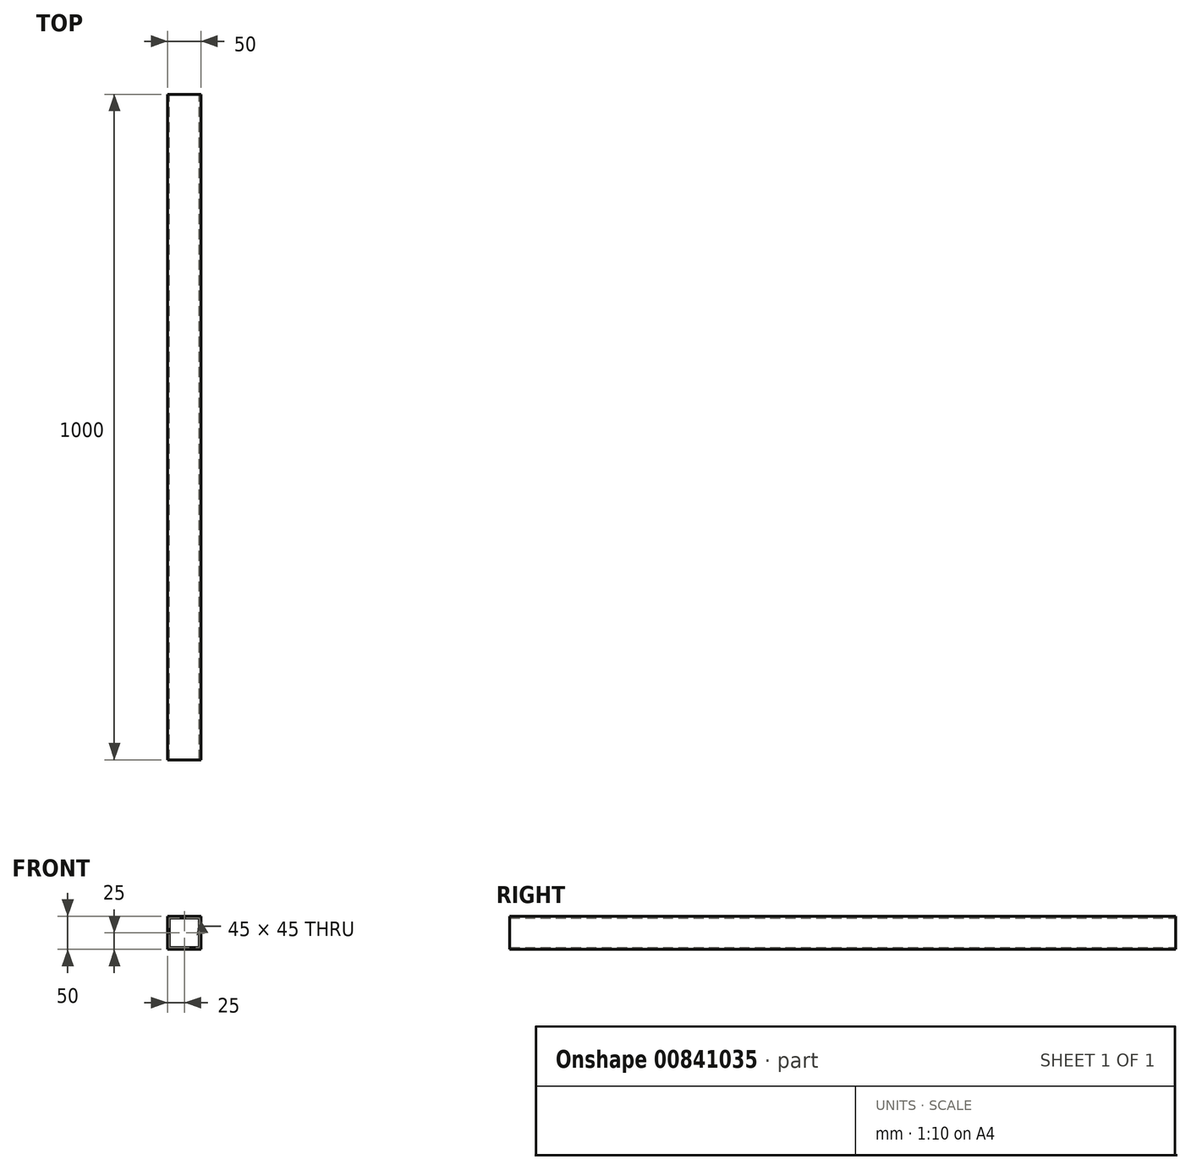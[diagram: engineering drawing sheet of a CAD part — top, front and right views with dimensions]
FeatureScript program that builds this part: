
annotation { "Feature Type Name" : "Feature", "Feature Type Description" : "" }
export const myFeature = defineFeature(function(context is Context, id is Id, definition is map)
    precondition{}
    {
        {
            var Q0;
            Q0=qCreatedBy(makeId("Front.planeOp"),FACE);
            var sketch = newSketch(context, id + "F0", { "sketchPlane" : qUnion([Q0])});
            skLineSegment(sketch, "E0.top", {"start": v(0, 25) * mm, "end": v(25, 25) * mm});
            skLineSegment(sketch, "E0.right", {"start": v(25, 0) * mm, "end": v(25, 25) * mm});
            skLineSegment(sketch, "E1.MirrorCS", {"start": v(0, 25) * mm, "end": v(-25, 25) * mm});
            skLineSegment(sketch, "E2.MirrorCS", {"start": v(-25, 0) * mm, "end": v(-25, 25) * mm});
            skLineSegment(sketch, "E3.MirrorCS", {"start": v(-25, 0) * mm, "end": v(-25, -25) * mm});
            skLineSegment(sketch, "E4.MirrorCS", {"start": v(0, -25) * mm, "end": v(-25, -25) * mm});
            skLineSegment(sketch, "E5.MirrorCS", {"start": v(0, -25) * mm, "end": v(25, -25) * mm});
            skLineSegment(sketch, "E6.MirrorCS", {"start": v(25, 0) * mm, "end": v(25, -25) * mm});
            skLineSegment(sketch, "E7", {"start": v(0, 0) * mm, "end": v(-75.09, 0) * mm});
            skSolve(sketch);
        }
        {
            var Q0;
            Q0 = qSketchRegion(id + "F0", true);
            extrude(context, id + "F1", {"entities" : qUnion([Q0]), "depth" : 1000 * mm, "offsetDistance" : 25 * mm});
        }
        {
            var Q0;
            Q0=makeQuery(id+"F1.opExtrude","CAP_FACE",FACE,{"disambiguationData":[OSD([sQuery(id+"F0.wireOp",EDGE,"E0.top"),sQuery(id+"F0.wireOp",EDGE,"E0.right"),sQuery(id+"F0.wireOp",EDGE,"E1.MirrorCS"),sQuery(id+"F0.wireOp",EDGE,"E2.MirrorCS"),sQuery(id+"F0.wireOp",EDGE,"E3.MirrorCS"),sQuery(id+"F0.wireOp",EDGE,"E4.MirrorCS"),sQuery(id+"F0.wireOp",EDGE,"E5.MirrorCS"),sQuery(id+"F0.wireOp",EDGE,"E6.MirrorCS")])],"isStart":false});
            var Q1;
            Q1=makeQuery(id+"F1.opExtrude","CAP_FACE",FACE,{"disambiguationData":[OSD([sQuery(id+"F0.wireOp",EDGE,"E0.top"),sQuery(id+"F0.wireOp",EDGE,"E0.right"),sQuery(id+"F0.wireOp",EDGE,"E1.MirrorCS"),sQuery(id+"F0.wireOp",EDGE,"E2.MirrorCS"),sQuery(id+"F0.wireOp",EDGE,"E3.MirrorCS"),sQuery(id+"F0.wireOp",EDGE,"E4.MirrorCS"),sQuery(id+"F0.wireOp",EDGE,"E5.MirrorCS"),sQuery(id+"F0.wireOp",EDGE,"E6.MirrorCS")])],"isStart":true});
            shell(context, id + "F2", {"entities" : qUnion([Q0, Q1]), "thickness" : 2.5 * mm});
        }
    });
